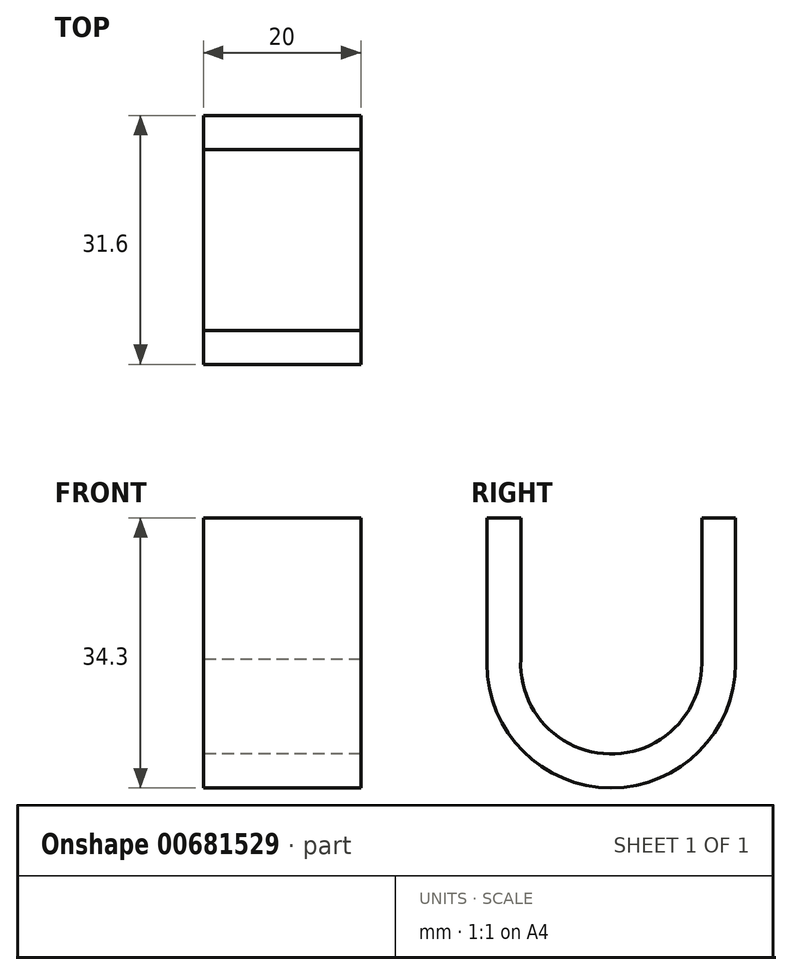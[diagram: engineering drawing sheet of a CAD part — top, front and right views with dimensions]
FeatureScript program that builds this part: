
annotation { "Feature Type Name" : "Feature", "Feature Type Description" : "" }
export const myFeature = defineFeature(function(context is Context, id is Id, definition is map)
    precondition{}
    {
        {
            var Q0;
            Q0=qCreatedBy(makeId("Right.planeOp"),FACE);
            var sketch = newSketch(context, id + "F0", { "sketchPlane" : qUnion([Q0])});
            skArc(sketch, "E0", {"start": v(-67.89, 12.41) * mm, "mid": v(-52.09, -3.39) * mm, "end": v(-36.29, 12.41) * mm});
            skLineSegment(sketch, "E1", {"start": v(-67.89, 12.41) * mm, "end": v(-67.89, 30.91) * mm});
            skLineSegment(sketch, "E2", {"start": v(-36.29, 12.41) * mm, "end": v(-36.29, 30.91) * mm});
            skArc(sketch, "E3", {"start": v(-63.58, 12.91) * mm, "mid": v(-52.34, 0.92) * mm, "end": v(-40.59, 12.41) * mm});
            skLineSegment(sketch, "E4", {"start": v(-67.89, 30.91) * mm, "end": v(-63.58, 30.91) * mm});
            skLineSegment(sketch, "E5", {"start": v(-63.58, 12.91) * mm, "end": v(-63.58, 30.91) * mm});
            skLineSegment(sketch, "E6", {"start": v(-40.59, 12.41) * mm, "end": v(-40.58, 30.91) * mm});
            skLineSegment(sketch, "E7.trimOffspring", {"start": v(-40.58, 30.91) * mm, "end": v(-36.29, 30.91) * mm});
            skSolve(sketch);
        }
        {
            var Q0;
            Q0=makeQuery(id+"F0.imprint","IMPRINT",FACE,{"disambiguationData":[TD([[makeQuery(id+"F0.imprint","IMPRINT",EDGE,{"derivedFrom":sQuery(id+"F0.wireOp",EDGE,"E0")}),1.0]])]});
            extrude(context, id + "F1", {"entities" : qUnion([Q0]), "depth" : 20 * mm, "offsetDistance" : 25 * mm});
        }
    });
